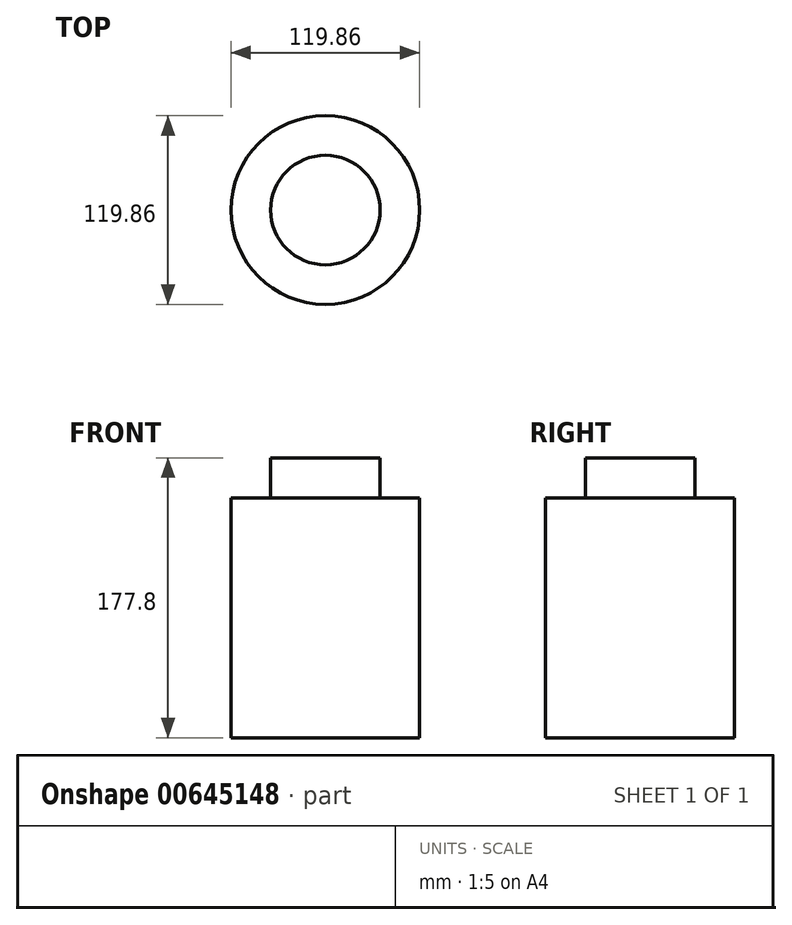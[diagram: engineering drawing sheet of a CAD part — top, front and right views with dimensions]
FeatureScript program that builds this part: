
annotation { "Feature Type Name" : "Feature", "Feature Type Description" : "" }
export const myFeature = defineFeature(function(context is Context, id is Id, definition is map)
    precondition{}
    {
        {
            var Q0;
            Q0=qCreatedBy(makeId("Top.planeOp"),FACE);
            var sketch = newSketch(context, id + "F0", { "sketchPlane" : qUnion([Q0])});
            skCircle(sketch, "E0", {"center": v(0, 0) * mm, "radius": 51.79 * mm});
            skCircle(sketch, "E1", {"center": v(0, 0) * mm, "radius": 59.93 * mm});
            skSolve(sketch);
        }
        {
            var Q0;
            Q0=makeQuery(id+"F0.imprint","IMPRINT",FACE,{"disambiguationData":[TD([[makeQuery(id+"F0.imprint","IMPRINT",EDGE,{"derivedFrom":sQuery(id+"F0.wireOp",EDGE,"E0")}),1.0]])]});
            var Q1;
            Q1=makeQuery(id+"F0.imprint","IMPRINT",FACE,{"disambiguationData":[TD([[makeQuery(id+"F0.imprint","IMPRINT",EDGE,{"derivedFrom":sQuery(id+"F0.wireOp",EDGE,"E0")}),-1.0]])]});
            var Q2;
            Q2=sQuery(id+"F0.wireOp",EDGE,"E0");
            extrude(context, id + "F1", {"entities" : qUnion([Q0, Q1]), "surfaceEntities" : qUnion([Q2]), "depth" : 127 * mm, "offsetDistance" : 25.4 * mm});
        }
        {
            var Q0;
            Q0=qCreatedBy(makeId("Top.planeOp"),FACE);
            var sketch = newSketch(context, id + "F2", { "sketchPlane" : qUnion([Q0])});
            skCircle(sketch, "E2", {"center": v(0, 0) * mm, "radius": 52.22 * mm});
            skSolve(sketch);
        }
        {
            var Q0;
            Q0=makeQuery(id+"F1.opExtrude","CAP_FACE",FACE,{"disambiguationData":[OSD([sQuery(id+"F0.wireOp",EDGE,"E1")])],"isStart":false});
            var Q1;
            Q1=sQuery(id+"F2.wireOp",EDGE,"E2");
            extrude(context, id + "F3", {"entities" : qUnion([Q0]), "operationType" : NewBodyOperationType.REMOVE, "surfaceEntities" : qUnion([Q1]), "oppositeDirection" : true, "depth" : 101.6 * mm, "offsetDistance" : 25.4 * mm});
        }
        {
            var Q0;
            Q0=makeQuery(id+"F3.boolean.opBoolean","COPY",FACE,{"derivedFrom":makeQuery(id+"F3.opExtrude","CAP_FACE",FACE,{"disambiguationData":[OSD([sQuery(id+"F0.wireOp",EDGE,"E1")])],"isStart":false})});
            extrude(context, id + "F4", {"entities" : qUnion([Q0]), "operationType" : NewBodyOperationType.ADD, "depth" : 127 * mm, "offsetDistance" : 25.4 * mm});
        }
        {
            var Q0;
            Q0=qCreatedBy(makeId("Top.planeOp"),FACE);
            var sketch = newSketch(context, id + "F5", { "sketchPlane" : qUnion([Q0])});
            skCircle(sketch, "E3", {"center": v(0, 0) * mm, "radius": 34.77 * mm});
            skSolve(sketch);
        }
        {
            var Q0;
            Q0 = qSketchRegion(id + "F5", true);
            extrude(context, id + "F6", {"entities" : qUnion([Q0]), "operationType" : NewBodyOperationType.ADD, "depth" : 177.8 * mm, "offsetDistance" : 25.4 * mm});
        }
    });
